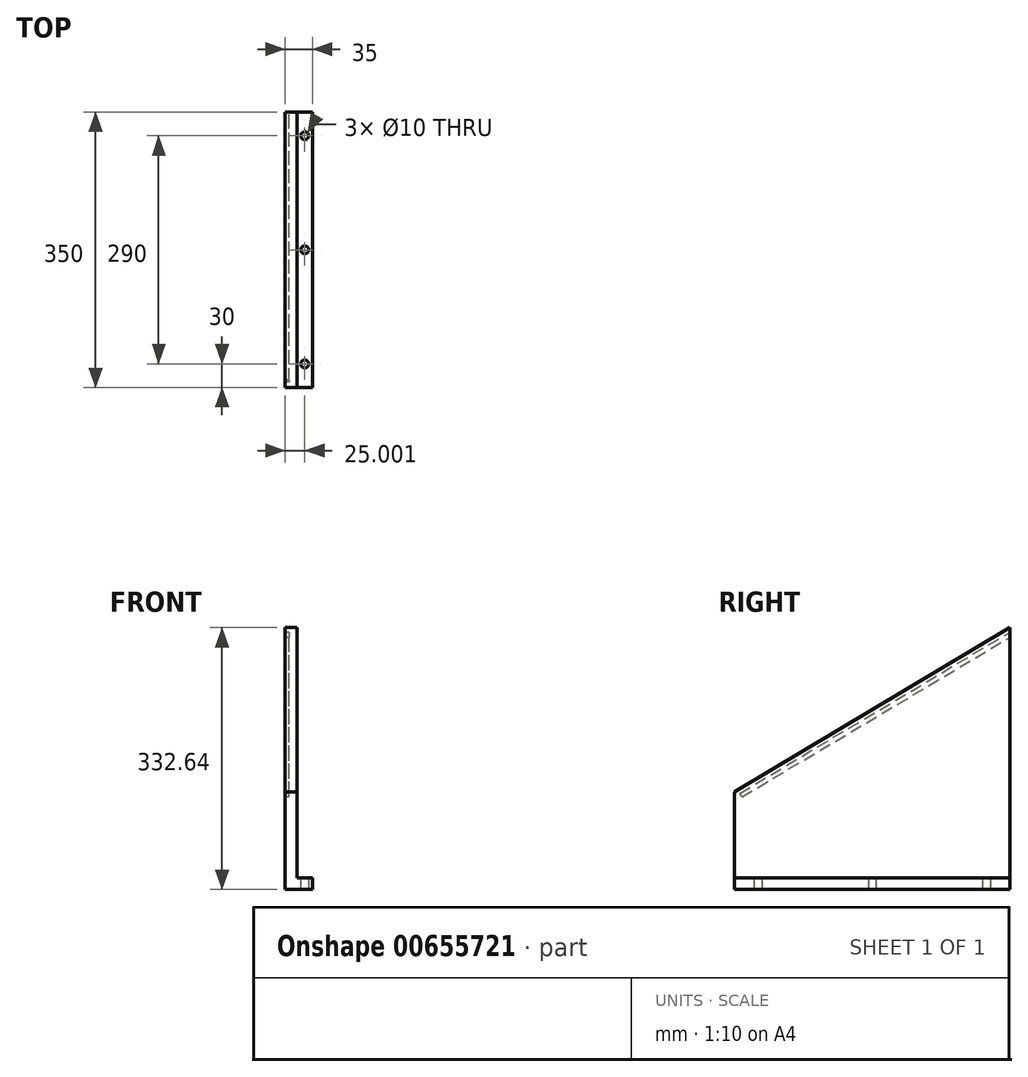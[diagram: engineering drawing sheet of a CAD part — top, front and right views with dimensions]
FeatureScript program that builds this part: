
annotation { "Feature Type Name" : "Feature", "Feature Type Description" : "" }
export const myFeature = defineFeature(function(context is Context, id is Id, definition is map)
    precondition{}
    {
        {
            var Q0;
            Q0=qCreatedBy(makeId("Top.planeOp"),FACE);
            var sketch = newSketch(context, id + "F0", { "sketchPlane" : qUnion([Q0])});
            skLineSegment(sketch, "E0.bottom", {"start": v(-75.23, -45.9) * mm, "end": v(-40.23, -45.9) * mm});
            skLineSegment(sketch, "E0.top", {"start": v(-75.23, 304.1) * mm, "end": v(-40.23, 304.1) * mm});
            skLineSegment(sketch, "E0.left", {"start": v(-75.23, -45.9) * mm, "end": v(-75.23, 304.1) * mm});
            skLineSegment(sketch, "E0.right", {"start": v(-40.23, -45.9) * mm, "end": v(-40.23, 304.1) * mm});
            skCircle(sketch, "E1", {"center": v(-50.23, -15.9) * mm, "radius": 5 * mm});
            skPoint(sketch, "E1.centerSnap0", {"position": v(-57.73, -45.9) * mm});
            skCircle(sketch, "E2", {"center": v(-50.23, 274.1) * mm, "radius": 5 * mm});
            skPoint(sketch, "E2.centerSnap0", {"position": v(-57.73, 304.1) * mm});
            skCircle(sketch, "E3", {"center": v(-50.23, 129.1) * mm, "radius": 5 * mm});
            skSolve(sketch);
        }
        {
            var Q0;
            Q0 = qSketchRegion(id + "F0", true);
            extrude(context, id + "F1", {"entities" : qUnion([Q0]), "depth" : 15 * mm, "offsetDistance" : 25 * mm});
        }
        {
            var Q0;
            Q0=makeQuery(id+"F1.opExtrude","CAP_FACE",FACE,{"disambiguationData":[OSD([sQuery(id+"F0.wireOp",EDGE,"E0.bottom"),sQuery(id+"F0.wireOp",EDGE,"E0.top"),sQuery(id+"F0.wireOp",EDGE,"E0.left"),sQuery(id+"F0.wireOp",EDGE,"E0.right"),sQuery(id+"F0.wireOp",EDGE,"E1"),sQuery(id+"F0.wireOp",EDGE,"E2"),sQuery(id+"F0.wireOp",EDGE,"E3")])],"isStart":false});
            var sketch = newSketch(context, id + "F2", { "sketchPlane" : qUnion([Q0])});
            skLineSegment(sketch, "E4.bottom", {"start": v(-75.23, -45.9) * mm, "end": v(-60.23, -45.9) * mm});
            skLineSegment(sketch, "E4.top", {"start": v(-75.23, 304.1) * mm, "end": v(-60.23, 304.1) * mm});
            skLineSegment(sketch, "E4.left", {"start": v(-75.23, -45.9) * mm, "end": v(-75.23, 304.1) * mm});
            skLineSegment(sketch, "E4.right", {"start": v(-60.23, -45.9) * mm, "end": v(-60.23, 304.1) * mm});
            skSolve(sketch);
        }
        {
            var Q0;
            Q0 = qSketchRegion(id + "F2", true);
            extrude(context, id + "F3", {"entities" : qUnion([Q0]), "operationType" : NewBodyOperationType.ADD, "depth" : 109 * mm, "offsetDistance" : 25 * mm});
        }
        {
            var Q0;
            Q0=makeQuery(id+"F3.opExtrude","SWEPT_FACE",FACE,{"disambiguationData":[OSD([sQuery(id+"F2.wireOp",EDGE,"E4.right")])]});
            var sketch = newSketch(context, id + "F4", { "sketchPlane" : qUnion([Q0])});
            skLineSegment(sketch, "E5", {"start": v(-45.9, 124) * mm, "end": v(254.73, 303.22) * mm});
            skLineSegment(sketch, "E6", {"start": v(-45.9, 124) * mm, "end": v(304.1, 124) * mm});
            skLineSegment(sketch, "E7", {"start": v(304.1, 124) * mm, "end": v(304.1, 332.64) * mm});
            skLineSegment(sketch, "E8", {"start": v(254.73, 303.22) * mm, "end": v(304.1, 332.64) * mm});
            skSolve(sketch);
        }
        {
            var Q0;
            Q0 = qSketchRegion(id + "F4", true);
            extrude(context, id + "F5", {"entities" : qUnion([Q0]), "operationType" : NewBodyOperationType.ADD, "oppositeDirection" : true, "depth" : 15 * mm, "offsetDistance" : 25 * mm});
        }
        {
            var Q0;
            Q0=makeQuery(id+"F5.boolean.opBoolean","MERGE",FACE,{"derivedFrom":[makeQuery(id+"F3.boolean.opBoolean","MERGE",FACE,{"derivedFrom":[makeQuery(id+"F1.opExtrude","SWEPT_FACE",FACE,{"disambiguationData":[OSD([sQuery(id+"F0.wireOp",EDGE,"E0.left")])]}),makeQuery(id+"F3.opExtrude","SWEPT_FACE",FACE,{"disambiguationData":[OSD([sQuery(id+"F2.wireOp",EDGE,"E4.left")])]})]}),makeQuery(id+"F5.opExtrude","CAP_FACE",FACE,{"disambiguationData":[OSD([sQuery(id+"F4.wireOp",EDGE,"E5"),sQuery(id+"F4.wireOp",EDGE,"E6"),sQuery(id+"F4.wireOp",EDGE,"E7"),sQuery(id+"F4.wireOp",EDGE,"E8")])],"isStart":false})]});
            var sketch = newSketch(context, id + "F6", { "sketchPlane" : qUnion([Q0])});
            skLineSegment(sketch, "E9.0", {"start": v(39.05, 122.27) * mm, "end": v(-304.1, 326.82) * mm});
            skLineSegment(sketch, "E10.0", {"start": v(36.24, 117.54) * mm, "end": v(-304.1, 320.42) * mm});
            skLineSegment(sketch, "E11.0", {"start": v(36.24, 117.54) * mm, "end": v(39.05, 122.27) * mm});
            skLineSegment(sketch, "E12", {"start": v(-304.1, 326.82) * mm, "end": v(-304.1, 320.42) * mm});
            skSolve(sketch);
        }
        {
            var Q0;
            Q0=makeQuery(id+"F6.imprint","IMPRINT",FACE,{"disambiguationData":[TD([[makeQuery(id+"F6.imprint","IMPRINT",EDGE,{"derivedFrom":sQuery(id+"F6.wireOp",EDGE,"E9.0")}),1.0]])]});
            extrude(context, id + "F7", {"entities" : qUnion([Q0]), "operationType" : NewBodyOperationType.REMOVE, "oppositeDirection" : true, "depth" : 5 * mm, "offsetDistance" : 25 * mm});
        }
    });
